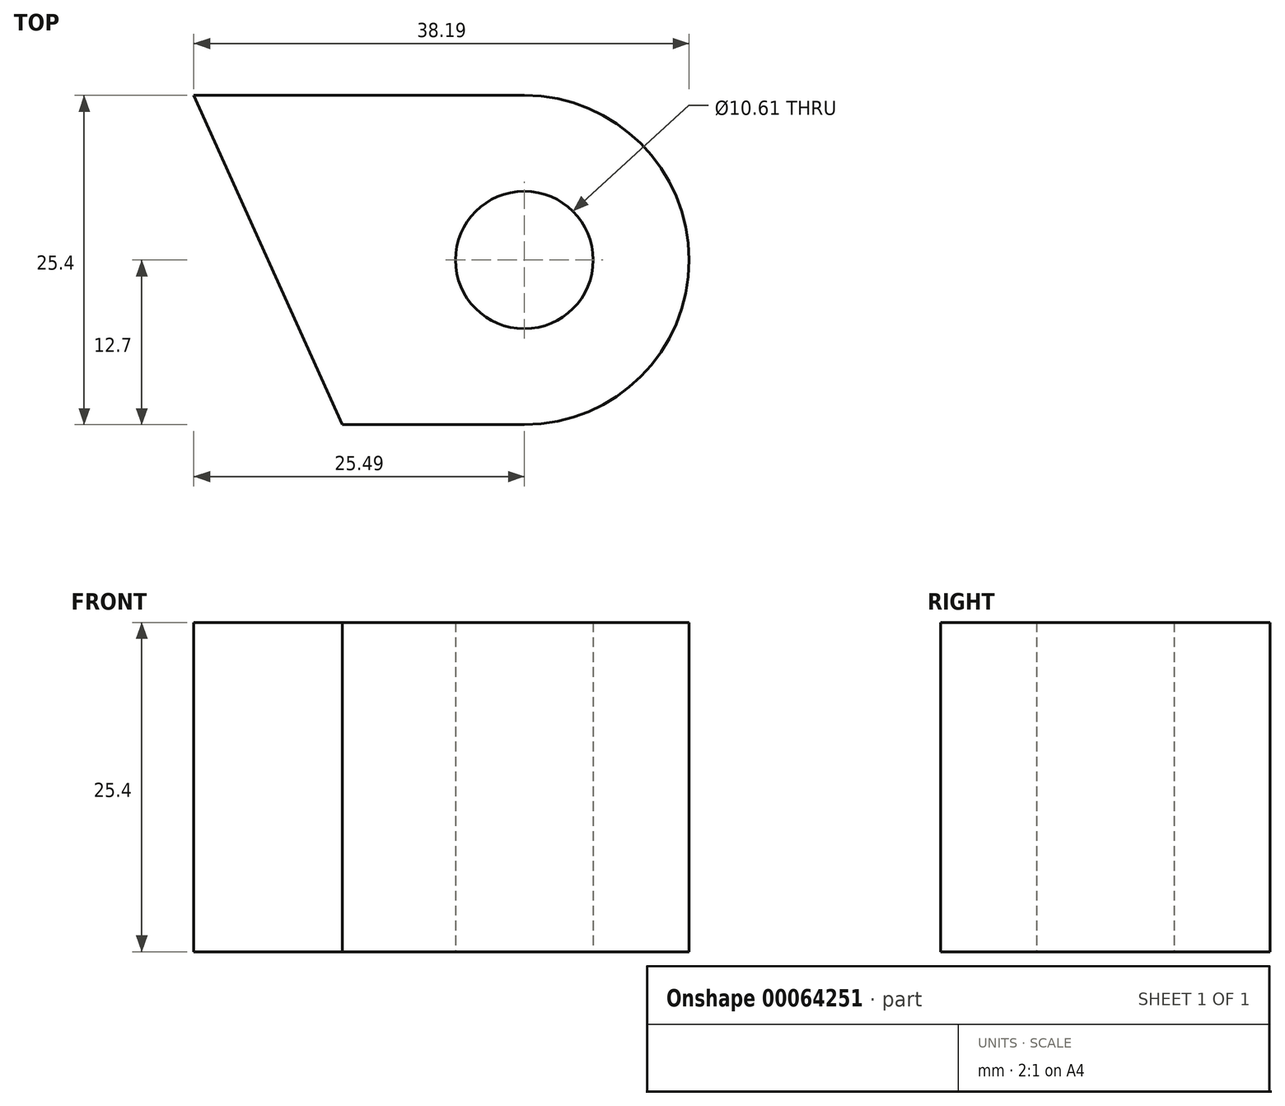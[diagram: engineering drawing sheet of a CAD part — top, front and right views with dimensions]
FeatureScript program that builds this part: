
annotation { "Feature Type Name" : "Feature", "Feature Type Description" : "" }
export const myFeature = defineFeature(function(context is Context, id is Id, definition is map)
    precondition{}
    {
        {
            var Q0;
            Q0=qCreatedBy(makeId("Top.planeOp"),FACE);
            var sketch = newSketch(context, id + "F0", { "sketchPlane" : qUnion([Q0])});
            skArc(sketch, "E0", {"start": v(0, -12.7) * mm, "mid": v(12.7, 0) * mm, "end": v(0, 12.7) * mm});
            skLineSegment(sketch, "E1", {"start": v(0, 12.7) * mm, "end": v(-25.49, 12.7) * mm});
            skLineSegment(sketch, "E2", {"start": v(0, -12.7) * mm, "end": v(-38.1, -12.7) * mm});
            skLineSegment(sketch, "E3", {"start": v(-38.1, -12.7) * mm, "end": v(-25.49, 12.7) * mm});
            skCircle(sketch, "E4", {"center": v(0, 0) * mm, "radius": 5.3 * mm});
            skSolve(sketch);
        }
        {
            var Q0;
            Q0=makeQuery(id+"F0.imprint","IMPRINT",FACE,{"disambiguationData":[TD([[makeQuery(id+"F0.imprint","IMPRINT",EDGE,{"derivedFrom":sQuery(id+"F0.wireOp",EDGE,"E0")}),1.0]])]});
            extrude(context, id + "F1", {"entities" : qUnion([Q0]), "depth" : 25.4 * mm});
        }
        {
            var Q0;
            Q0=makeQuery(id+"F1.opExtrude","CAP_FACE",FACE,{"disambiguationData":[OSD([sQuery(id+"F0.wireOp",EDGE,"E0"),sQuery(id+"F0.wireOp",EDGE,"E1"),sQuery(id+"F0.wireOp",EDGE,"E2"),sQuery(id+"F0.wireOp",EDGE,"E3")])],"isStart":false});
            var sketch = newSketch(context, id + "F2", { "sketchPlane" : qUnion([Q0])});
            skLineSegment(sketch, "E5", {"start": v(-25.49, 12.7) * mm, "end": v(-14.04, -12.7) * mm});
            skSolve(sketch);
        }
        {
            var Q0;
            {var subQ0=sQuery(id+"F2.wireOp",EDGE,"E5");Q0=makeQuery(id+"F2.imprint","IMPRINT",FACE,{"disambiguationData":[TD([[makeQuery(id+"F2.imprint","IMPRINT",EDGE,{"derivedFrom":subQ0}),-1.0]])]});}
            extrude(context, id + "F3", {"entities" : qUnion([Q0]), "operationType" : NewBodyOperationType.REMOVE, "oppositeDirection" : true, "depth" : 25.4 * mm});
        }
    });
